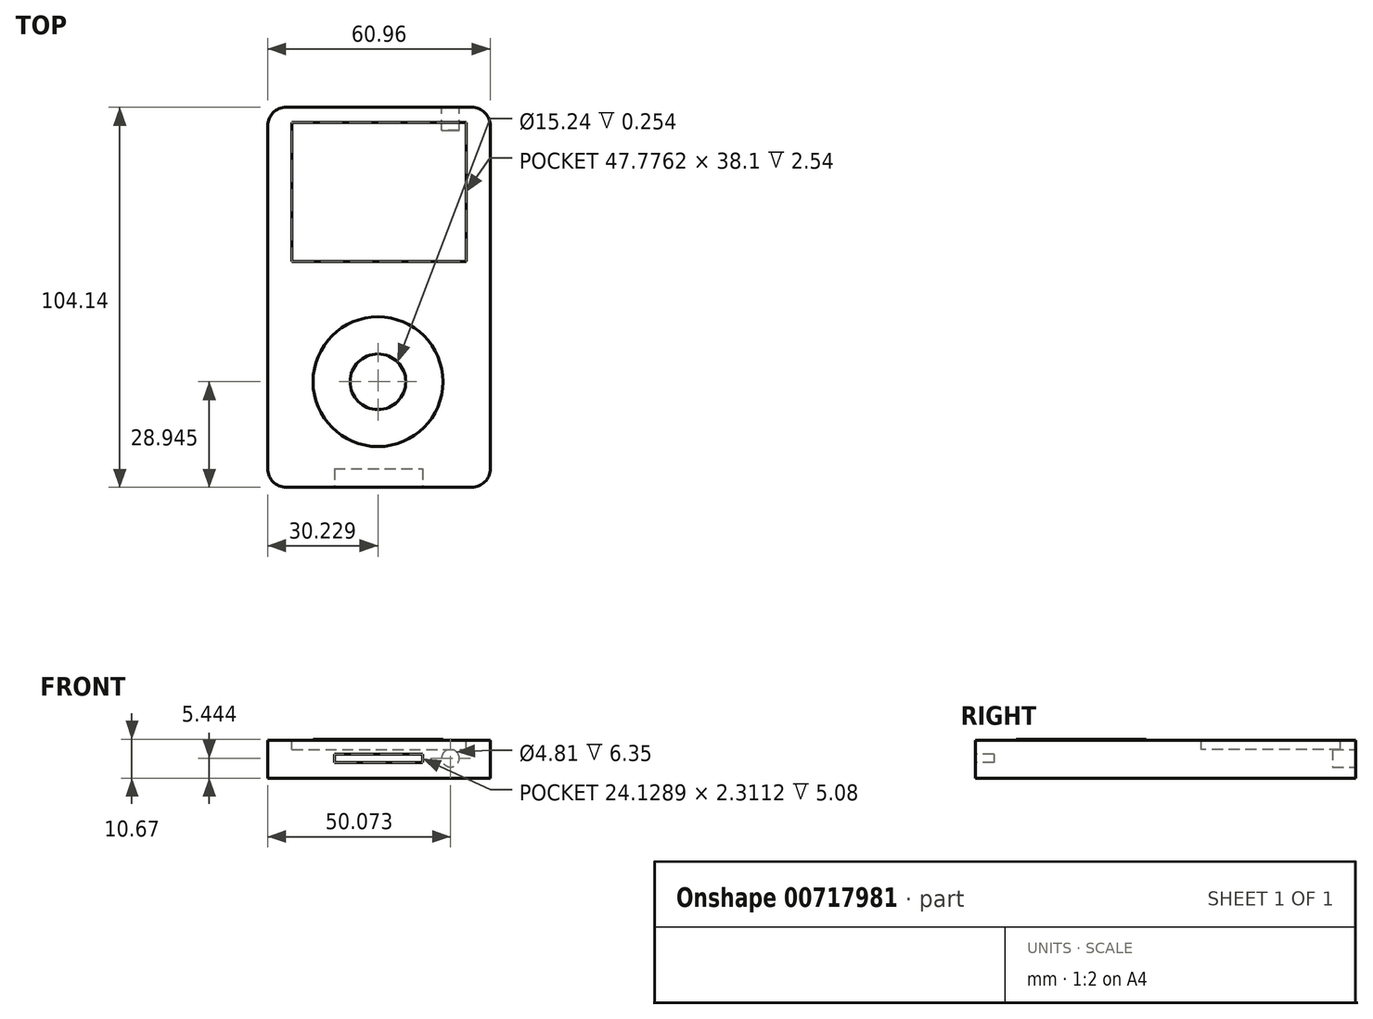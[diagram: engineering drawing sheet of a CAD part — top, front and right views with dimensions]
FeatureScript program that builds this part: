
annotation { "Feature Type Name" : "Feature", "Feature Type Description" : "" }
export const myFeature = defineFeature(function(context is Context, id is Id, definition is map)
    precondition{}
    {
        {
            var Q0;
            Q0=qCreatedBy(makeId("Top.planeOp"),FACE);
            var sketch = newSketch(context, id + "F0", { "sketchPlane" : qUnion([Q0])});
            skLineSegment(sketch, "E0.bottom", {"start": v(-39.18, 55.9) * mm, "end": v(21.78, 55.9) * mm});
            skLineSegment(sketch, "E0.top", {"start": v(-39.18, -48.25) * mm, "end": v(21.78, -48.25) * mm});
            skLineSegment(sketch, "E0.left", {"start": v(-39.18, 55.9) * mm, "end": v(-39.18, -48.25) * mm});
            skLineSegment(sketch, "E0.right", {"start": v(21.78, 55.9) * mm, "end": v(21.78, -48.25) * mm});
            skSolve(sketch);
        }
        {
            var Q0;
            Q0=makeQuery(id+"F0.imprint","IMPRINT",FACE,{"disambiguationData":[TD([[makeQuery(id+"F0.imprint","IMPRINT",EDGE,{"derivedFrom":sQuery(id+"F0.wireOp",EDGE,"E0.bottom")}),-1.0]])]});
            extrude(context, id + "F1", {"entities" : qUnion([Q0]), "depth" : 10.4 * mm, "offsetDistance" : 25.4 * mm});
        }
        {
            var Q0;
            Q0=makeQuery(id+"F1.opExtrude","SWEPT_EDGE",EDGE,{"disambiguationData":[OSD([sQuery(id+"F0.wireOp",EDGE,"E0.bottom"),sQuery(id+"F0.wireOp",EDGE,"E0.right")])]});
            fillet(context, id + "F2", {"entities" : qUnion([Q0]), "radius" : 5.08 * mm, "tangentPropagation" : true, "allowEdgeOverflow" : false});
        }
        {
            var Q0;
            Q0=makeQuery(id+"F1.opExtrude","SWEPT_EDGE",EDGE,{"disambiguationData":[OSD([sQuery(id+"F0.wireOp",EDGE,"E0.bottom"),sQuery(id+"F0.wireOp",EDGE,"E0.left")])]});
            fillet(context, id + "F3", {"entities" : qUnion([Q0]), "radius" : 5.08 * mm, "tangentPropagation" : true, "allowEdgeOverflow" : false});
        }
        {
            var Q0;
            Q0=makeQuery(id+"F1.opExtrude","SWEPT_EDGE",EDGE,{"disambiguationData":[OSD([sQuery(id+"F0.wireOp",EDGE,"E0.top"),sQuery(id+"F0.wireOp",EDGE,"E0.right")])]});
            fillet(context, id + "F4", {"entities" : qUnion([Q0]), "radius" : 5.08 * mm, "tangentPropagation" : true, "allowEdgeOverflow" : false});
        }
        {
            var Q0;
            Q0=makeQuery(id+"F1.opExtrude","SWEPT_EDGE",EDGE,{"disambiguationData":[OSD([sQuery(id+"F0.wireOp",EDGE,"E0.top"),sQuery(id+"F0.wireOp",EDGE,"E0.left")])]});
            fillet(context, id + "F5", {"entities" : qUnion([Q0]), "radius" : 5.08 * mm, "tangentPropagation" : true, "allowEdgeOverflow" : false});
        }
        {
            var Q0;
            Q0=makeQuery(id+"F1.opExtrude","CAP_FACE",FACE,{"disambiguationData":[OSD([sQuery(id+"F0.wireOp",EDGE,"E0.bottom"),sQuery(id+"F0.wireOp",EDGE,"E0.top"),sQuery(id+"F0.wireOp",EDGE,"E0.left"),sQuery(id+"F0.wireOp",EDGE,"E0.right")])],"isStart":false});
            var sketch = newSketch(context, id + "F6", { "sketchPlane" : qUnion([Q0])});
            skLineSegment(sketch, "E1.bottom", {"start": v(-32.52, 51.7) * mm, "end": v(15.26, 51.7) * mm});
            skLineSegment(sketch, "E1.top", {"start": v(-32.52, 13.6) * mm, "end": v(15.26, 13.6) * mm});
            skLineSegment(sketch, "E1.left", {"start": v(-32.52, 51.7) * mm, "end": v(-32.52, 13.6) * mm});
            skLineSegment(sketch, "E1.right", {"start": v(15.26, 51.7) * mm, "end": v(15.26, 13.6) * mm});
            skSolve(sketch);
        }
        {
            var Q0;
            Q0=makeQuery(id+"F6.imprint","IMPRINT",FACE,{"disambiguationData":[TD([[makeQuery(id+"F6.imprint","IMPRINT",EDGE,{"derivedFrom":sQuery(id+"F6.wireOp",EDGE,"E1.bottom")}),1.0]])]});
            var sketch = newSketch(context, id + "F7", { "sketchPlane" : qUnion([Q0])});
            skCircle(sketch, "E2", {"center": v(-8.95, -19.3) * mm, "radius": 17.78 * mm});
            skCircle(sketch, "E3", {"center": v(-8.95, -19.3) * mm, "radius": 7.62 * mm});
            skSolve(sketch);
        }
        {
            var Q0;
            Q0 = qSketchRegion(id + "F6", true);
            extrude(context, id + "F8", {"entities" : qUnion([Q0]), "operationType" : NewBodyOperationType.REMOVE, "oppositeDirection" : true, "depth" : 2.54 * mm, "offsetDistance" : 25.4 * mm});
        }
        {
            var Q0;
            Q0 = qSketchRegion(id + "F7", true);
            extrude(context, id + "F9", {"entities" : qUnion([Q0]), "operationType" : NewBodyOperationType.ADD, "depth" : 0.25 * mm, "offsetDistance" : 25.4 * mm});
        }
        {
            var Q0;
            Q0=makeQuery(id+"F1.opExtrude","SWEPT_FACE",FACE,{"disambiguationData":[OSD([sQuery(id+"F0.wireOp",EDGE,"E0.bottom")])]});
            var sketch = newSketch(context, id + "F10", { "sketchPlane" : qUnion([Q0])});
            skCircle(sketch, "E4", {"center": v(-10.9, 5.44) * mm, "radius": 2.4 * mm});
            skSolve(sketch);
        }
        {
            var Q0;
            Q0 = qSketchRegion(id + "F10", true);
            extrude(context, id + "F11", {"entities" : qUnion([Q0]), "operationType" : NewBodyOperationType.REMOVE, "oppositeDirection" : true, "depth" : 6.35 * mm, "offsetDistance" : 25.4 * mm});
        }
        {
            var Q0;
            Q0=makeQuery(id+"F1.opExtrude","SWEPT_FACE",FACE,{"disambiguationData":[OSD([sQuery(id+"F0.wireOp",EDGE,"E0.top")])]});
            var sketch = newSketch(context, id + "F12", { "sketchPlane" : qUnion([Q0])});
            skLineSegment(sketch, "E5.bottom", {"start": v(-20.9, 6.56) * mm, "end": v(3.22, 6.56) * mm});
            skLineSegment(sketch, "E5.top", {"start": v(-20.9, 4.24) * mm, "end": v(3.22, 4.24) * mm});
            skLineSegment(sketch, "E5.left", {"start": v(-20.9, 6.56) * mm, "end": v(-20.9, 4.24) * mm});
            skLineSegment(sketch, "E5.right", {"start": v(3.22, 6.56) * mm, "end": v(3.22, 4.24) * mm});
            skSolve(sketch);
        }
        {
            var Q0;
            Q0 = qSketchRegion(id + "F12", true);
            extrude(context, id + "F13", {"entities" : qUnion([Q0]), "operationType" : NewBodyOperationType.REMOVE, "oppositeDirection" : true, "depth" : 5.08 * mm, "offsetDistance" : 25.4 * mm});
        }
    });
